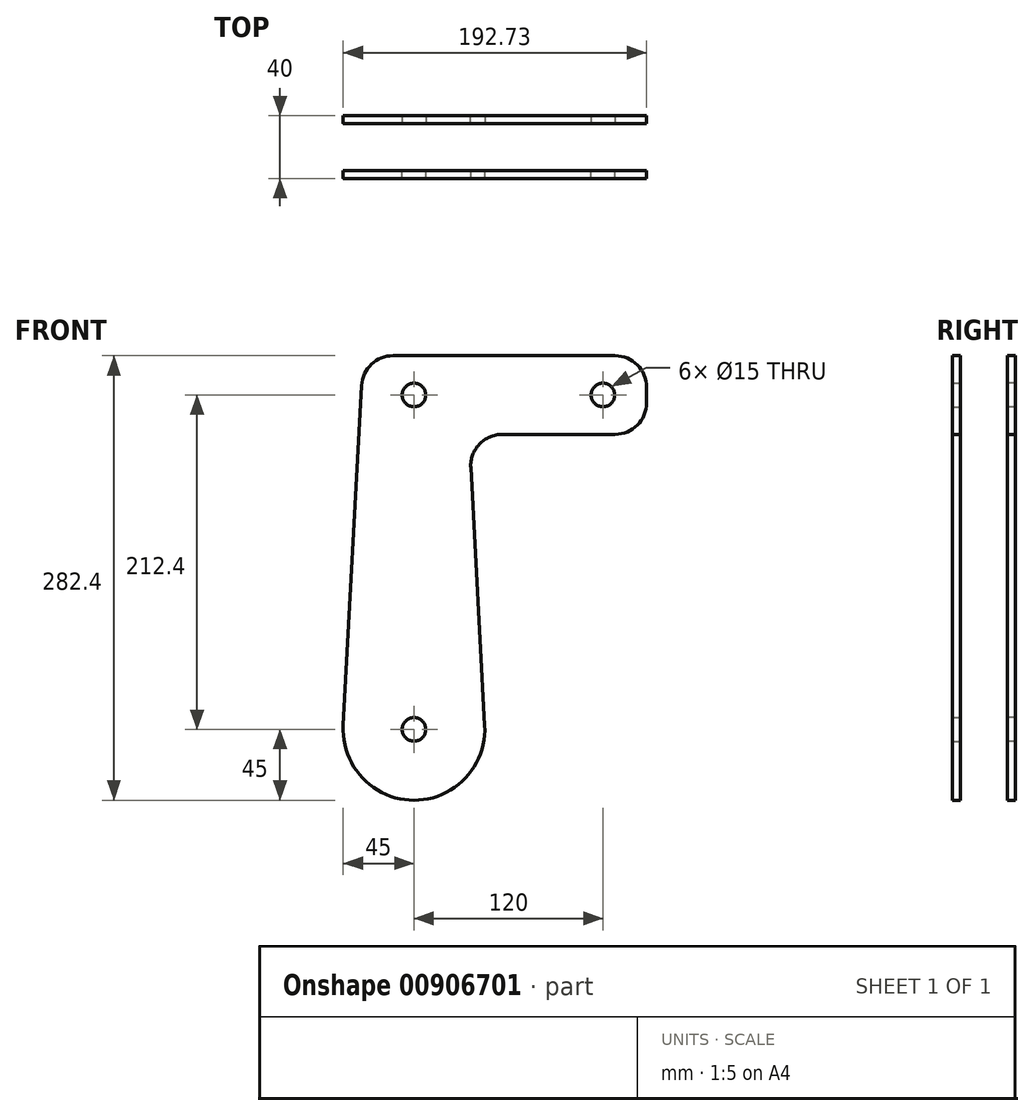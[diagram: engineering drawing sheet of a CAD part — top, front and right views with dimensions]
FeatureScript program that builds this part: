
annotation { "Feature Type Name" : "Feature", "Feature Type Description" : "" }
export const myFeature = defineFeature(function(context is Context, id is Id, definition is map)
    precondition{}
    {
        {
            var Q0;
            Q0=qCreatedBy(makeId("Front.planeOp"),FACE);
            var sketch = newSketch(context, id + "F0", { "sketchPlane" : qUnion([Q0])});
            skCircle(sketch, "E0", {"center": v(0, 0) * mm, "radius": 7.5 * mm});
            skCircle(sketch, "E1", {"center": v(0, 0) * mm, "radius": 45 * mm});
            skCircle(sketch, "E2", {"center": v(0, 212.4) * mm, "radius": 7.5 * mm});
            skLineSegment(sketch, "E3", {"start": v(-32.27, 237.4) * mm, "end": v(-45.07, 0) * mm});
            skLineSegment(sketch, "E4", {"start": v(-32.27, 237.4) * mm, "end": v(147.73, 237.4) * mm});
            skLineSegment(sketch, "E5", {"start": v(147.73, 237.4) * mm, "end": v(147.73, 187.4) * mm});
            skLineSegment(sketch, "E6", {"start": v(147.73, 187.4) * mm, "end": v(34.92, 187.4) * mm});
            skLineSegment(sketch, "E7", {"start": v(34.92, 187.4) * mm, "end": v(45.07, 0) * mm});
            skCircle(sketch, "E8", {"center": v(120, 212.4) * mm, "radius": 7.5 * mm});
            skSolve(sketch);
        }
        {
            var Q0;
            Q0=makeQuery(id+"F0.imprint","IMPRINT",FACE,{"disambiguationData":[TD([[makeQuery(id+"F0.imprint","IMPRINT",EDGE,{"derivedFrom":sQuery(id+"F0.wireOp",EDGE,"E2")}),-1.0]])]});
            var Q1;
            Q1=makeQuery(id+"F0.imprint","IMPRINT",FACE,{"disambiguationData":[TD([[makeQuery(id+"F0.imprint","IMPRINT",EDGE,{"derivedFrom":sQuery(id+"F0.wireOp",EDGE,"E0")}),-1.0]])]});
            extrude(context, id + "F1", {"entities" : qUnion([Q0, Q1]), "depth" : 5 * mm, "offsetDistance" : 25 * mm});
        }
        {
            var Q0;
            Q0=makeQuery(id+"F1.opExtrude","SWEPT_EDGE",EDGE,{"disambiguationData":[OSD([sQuery(id+"F0.wireOp",EDGE,"E4"),sQuery(id+"F0.wireOp",EDGE,"E5")])]});
            fillet(context, id + "F2", {"entities" : qUnion([Q0]), "radius" : 20 * mm, "tangentPropagation" : true, "allowEdgeOverflow" : false});
        }
        {
            var Q0;
            Q0=makeQuery(id+"F1.opExtrude","SWEPT_EDGE",EDGE,{"disambiguationData":[OSD([sQuery(id+"F0.wireOp",EDGE,"E5"),sQuery(id+"F0.wireOp",EDGE,"E6")])]});
            fillet(context, id + "F3", {"entities" : qUnion([Q0]), "radius" : 20 * mm, "tangentPropagation" : true, "allowEdgeOverflow" : false});
        }
        {
            var Q0;
            Q0=makeQuery(id+"F1.opExtrude","SWEPT_EDGE",EDGE,{"disambiguationData":[OSD([sQuery(id+"F0.wireOp",EDGE,"E3"),sQuery(id+"F0.wireOp",EDGE,"E4")])]});
            fillet(context, id + "F4", {"entities" : qUnion([Q0]), "radius" : 20 * mm, "tangentPropagation" : true, "allowEdgeOverflow" : false});
        }
        {
            var Q0;
            Q0=makeQuery(id+"F1.opExtrude","SWEPT_EDGE",EDGE,{"disambiguationData":[OSD([sQuery(id+"F0.wireOp",EDGE,"E6"),sQuery(id+"F0.wireOp",EDGE,"E7")])]});
            fillet(context, id + "F5", {"entities" : qUnion([Q0]), "radius" : 20 * mm, "tangentPropagation" : true, "allowEdgeOverflow" : false});
        }
        {
            var Q0;
            Q0=qCreatedBy(makeId("Front.planeOp"),FACE);
            cPlane(context, id + "F6", {"entities" : qUnion([Q0]), "cplaneType" : CPlaneType.OFFSET, "offset" : 15 * mm, "oppositeDirection" : true, "width" : 150 * mm, "height" : 150 * mm});
        }
        {
            var Q0;
            Q0=makeQuery(id+"F1.opExtrude","SWEPT_BODY",BODY,{"disambiguationData":[OSD([sQuery(id+"F0.wireOp",EDGE,"E0"),sQuery(id+"F0.wireOp",EDGE,"E1"),sQuery(id+"F0.wireOp",EDGE,"E2"),sQuery(id+"F0.wireOp",EDGE,"E3"),sQuery(id+"F0.wireOp",EDGE,"E4"),sQuery(id+"F0.wireOp",EDGE,"E5"),sQuery(id+"F0.wireOp",EDGE,"E6"),sQuery(id+"F0.wireOp",EDGE,"E7"),sQuery(id+"F0.wireOp",EDGE,"E8")])]});
            var Q1;
            Q1=qCreatedBy(id+"F6.planeOp",FACE);
            mirror(context, id + "F7", {"entities" : qUnion([Q0]), "mirrorPlane" : qUnion([Q1])});
        }
    });
